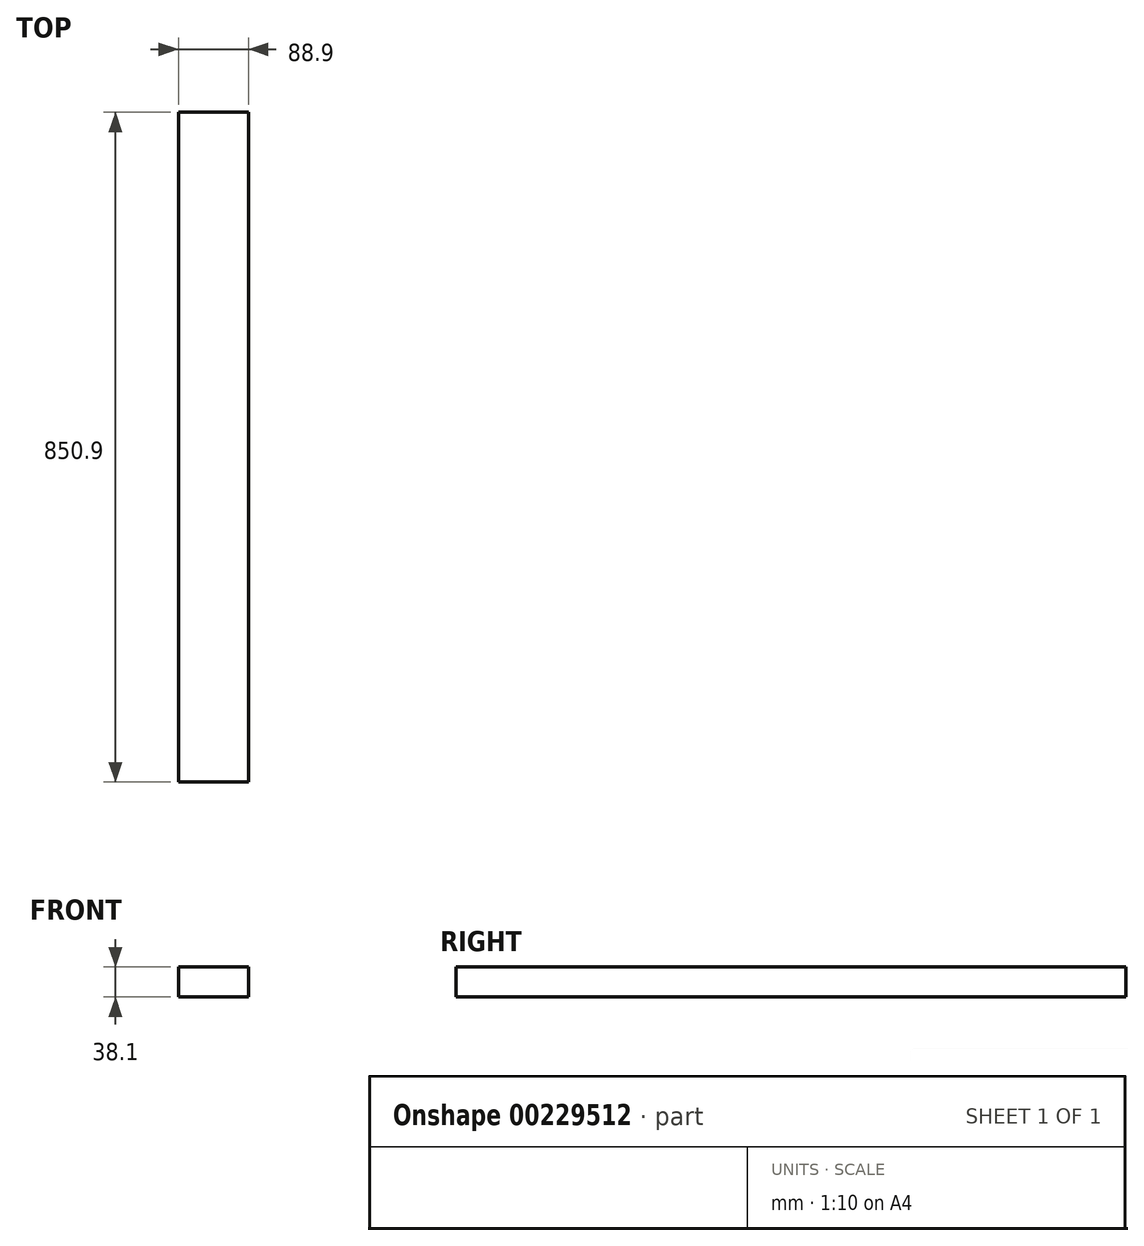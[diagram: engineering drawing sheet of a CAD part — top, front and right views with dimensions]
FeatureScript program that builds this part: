
annotation { "Feature Type Name" : "Feature", "Feature Type Description" : "" }
export const myFeature = defineFeature(function(context is Context, id is Id, definition is map)
    precondition{}
    {
        {
            var Q0;
            Q0=qCreatedBy(makeId("Front.planeOp"),FACE);
            var sketch = newSketch(context, id + "F0", { "sketchPlane" : qUnion([Q0])});
            skLineSegment(sketch, "E0.bottom", {"start": v(0, 0) * mm, "end": v(88.9, 0) * mm});
            skLineSegment(sketch, "E0.top", {"start": v(0, -38.1) * mm, "end": v(88.9, -38.1) * mm});
            skLineSegment(sketch, "E0.left", {"start": v(0, 0) * mm, "end": v(0, -38.1) * mm});
            skLineSegment(sketch, "E0.right", {"start": v(88.9, 0) * mm, "end": v(88.9, -38.1) * mm});
            skSolve(sketch);
        }
        {
            var Q0;
            Q0=qSketchRegion(id+"F0",true);
            extrude(context, id + "F1", {"entities" : qUnion([Q0]), "depth" : 850.9 * mm});
        }
    });
